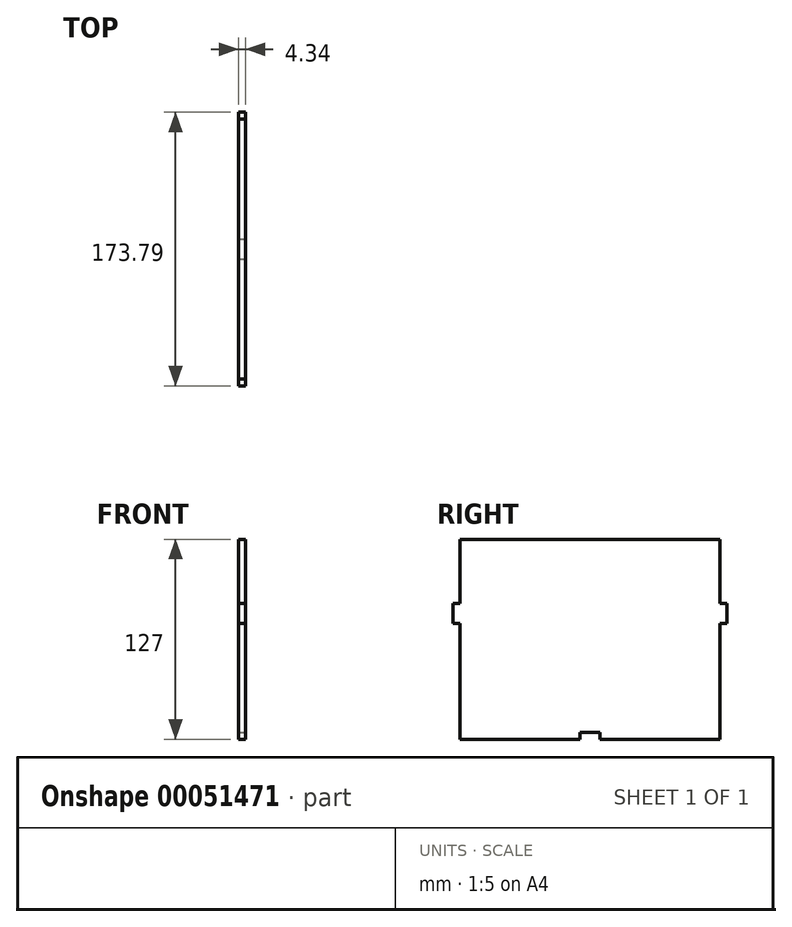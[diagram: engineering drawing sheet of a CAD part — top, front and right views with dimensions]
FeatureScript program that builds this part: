
annotation { "Feature Type Name" : "Feature", "Feature Type Description" : "" }
export const myFeature = defineFeature(function(context is Context, id is Id, definition is map)
    precondition{}
    {
        {
            var Q0;
            Q0=qCreatedBy(makeId("Right.planeOp"),FACE);
            var sketch = newSketch(context, id + "F0", { "sketchPlane" : qUnion([Q0])});
            skLineSegment(sketch, "E0.bottom", {"start": v(-53.18, 79.9) * mm, "end": v(111.92, 79.9) * mm});
            skLineSegment(sketch, "E0.top", {"start": v(-53.18, -47.1) * mm, "end": v(111.92, -47.1) * mm});
            skLineSegment(sketch, "E0.left", {"start": v(-53.18, 79.9) * mm, "end": v(-53.18, -47.1) * mm});
            skLineSegment(sketch, "E0.right", {"start": v(111.92, 79.9) * mm, "end": v(111.92, -47.1) * mm});
            skLineSegment(sketch, "E1.bottom", {"start": v(-53.18, 39.27) * mm, "end": v(-57.52, 39.27) * mm});
            skLineSegment(sketch, "E1.top", {"start": v(-53.18, 26.57) * mm, "end": v(-57.52, 26.57) * mm});
            skLineSegment(sketch, "E1.left", {"start": v(-53.18, 39.27) * mm, "end": v(-53.18, 26.57) * mm});
            skLineSegment(sketch, "E1.right", {"start": v(-57.52, 39.27) * mm, "end": v(-57.52, 26.57) * mm});
            skLineSegment(sketch, "E2.0", {"start": v(-53.18, 39.25) * mm, "end": v(111.92, 39.25) * mm, "construction": true});
            skLineSegment(sketch, "E3.0", {"start": v(23.02, 79.9) * mm, "end": v(23.02, -47.1) * mm, "construction": true});
            skLineSegment(sketch, "E4.0", {"start": v(35.72, 79.9) * mm, "end": v(35.72, -47.1) * mm, "construction": true});
            skLineSegment(sketch, "E5.bottom", {"start": v(23.02, -47.1) * mm, "end": v(35.72, -47.1) * mm});
            skLineSegment(sketch, "E5.top", {"start": v(23.02, -42.76) * mm, "end": v(35.72, -42.76) * mm});
            skLineSegment(sketch, "E5.left", {"start": v(23.02, -47.1) * mm, "end": v(23.02, -42.76) * mm});
            skLineSegment(sketch, "E5.right", {"start": v(35.72, -47.1) * mm, "end": v(35.72, -42.76) * mm});
            skLineSegment(sketch, "E6.0", {"start": v(29.37, 79.9) * mm, "end": v(29.37, -47.1) * mm, "construction": true});
            skLineSegment(sketch, "E7.MirrorCS", {"start": v(116.27, 39.27) * mm, "end": v(116.27, 26.57) * mm});
            skLineSegment(sketch, "E8.MirrorCS", {"start": v(111.92, 39.27) * mm, "end": v(116.27, 39.27) * mm});
            skLineSegment(sketch, "E9.MirrorCS", {"start": v(111.92, 26.57) * mm, "end": v(116.27, 26.57) * mm});
            skLineSegment(sketch, "E10.MirrorCS", {"start": v(111.92, 39.27) * mm, "end": v(111.92, 26.57) * mm});
            skSolve(sketch);
        }
        {
            var Q0;
            Q0 = qSketchRegion(id + "F0", true);
            extrude(context, id + "F1", {"entities" : qUnion([Q0]), "oppositeDirection" : true, "depth" : 4.34 * mm});
        }
        {
            var Q0;
            Q0=qCreatedBy(makeId("Right.planeOp"),FACE);
            var sketch = newSketch(context, id + "F2", { "sketchPlane" : qUnion([Q0])});
            skLineSegment(sketch, "E11.0", {"start": v(23.02, 26.57) * mm, "end": v(23.02, -47.1) * mm, "construction": true});
            skLineSegment(sketch, "E12.0", {"start": v(35.72, 79.9) * mm, "end": v(35.72, -47.1) * mm, "construction": true});
            skLineSegment(sketch, "E13.0", {"start": v(23.02, 79.9) * mm, "end": v(23.02, 39.27) * mm, "construction": true});
            skLineSegment(sketch, "E14.0", {"start": v(23.02, 39.27) * mm, "end": v(23.02, 26.57) * mm, "construction": true});
            skLineSegment(sketch, "E15.bottom", {"start": v(23.02, -42.76) * mm, "end": v(35.72, -42.76) * mm});
            skLineSegment(sketch, "E15.top", {"start": v(23.02, -47.1) * mm, "end": v(35.72, -47.1) * mm});
            skLineSegment(sketch, "E15.left", {"start": v(23.02, -42.76) * mm, "end": v(23.02, -47.1) * mm});
            skLineSegment(sketch, "E15.right", {"start": v(35.72, -42.76) * mm, "end": v(35.72, -47.1) * mm});
            skSolve(sketch);
        }
        {
            var Q0;
            Q0 = qSketchRegion(id + "F2", true);
            extrude(context, id + "F3", {"entities" : qUnion([Q0]), "operationType" : NewBodyOperationType.REMOVE, "endBound" : BoundingType.THROUGH_ALL, "oppositeDirection" : true, "depth" : 25.4 * mm});
        }
    });
